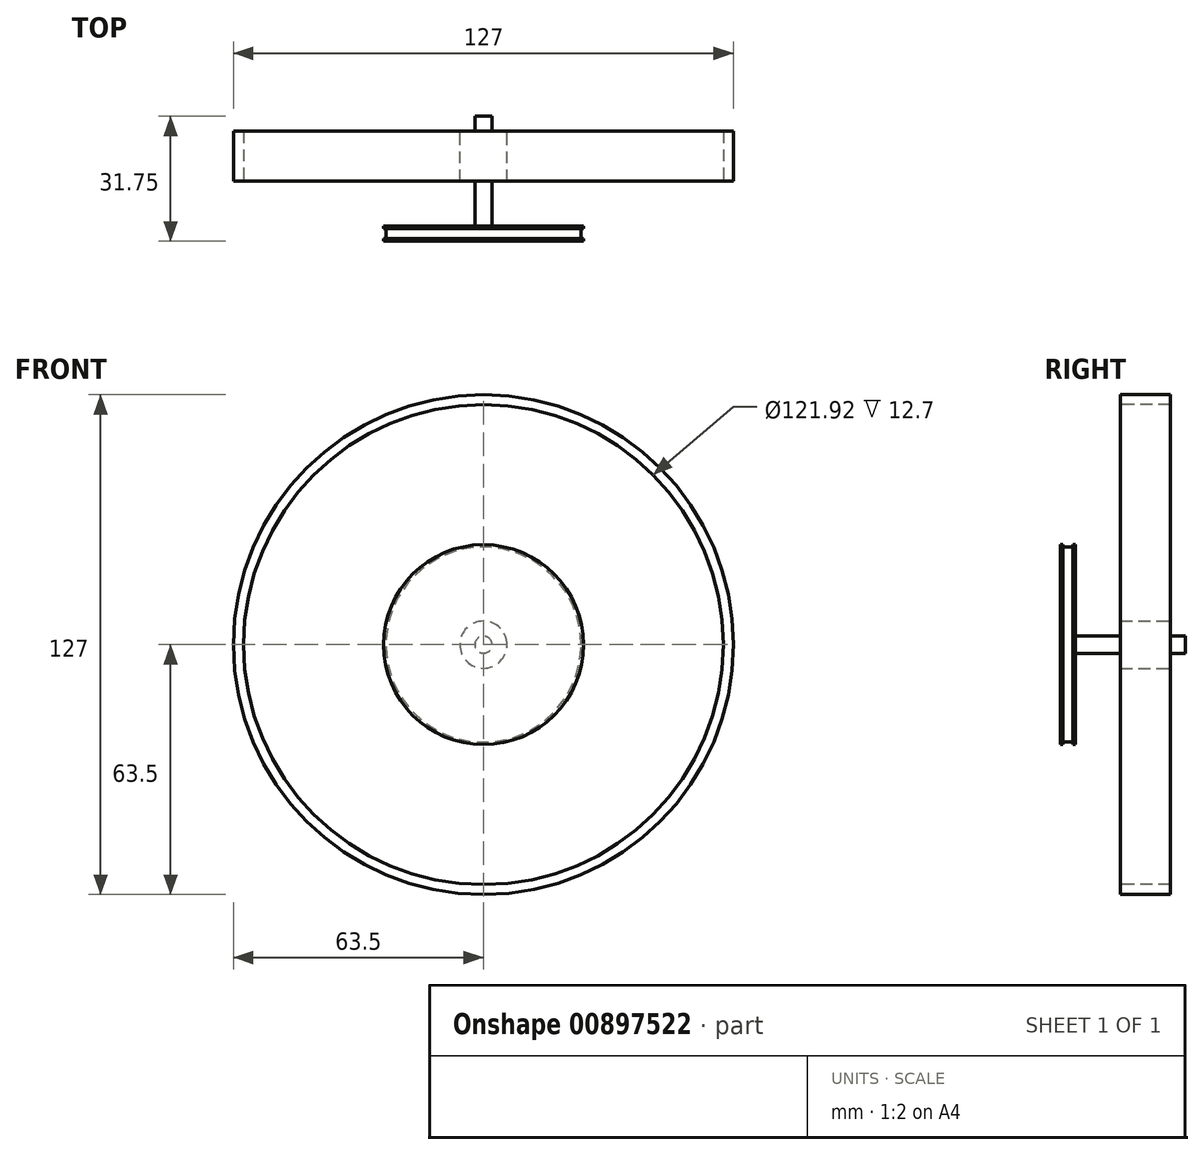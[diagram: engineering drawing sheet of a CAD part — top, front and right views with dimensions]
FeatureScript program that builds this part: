
annotation { "Feature Type Name" : "Feature", "Feature Type Description" : "" }
export const myFeature = defineFeature(function(context is Context, id is Id, definition is map)
    precondition{}
    {
        {
            var Q0;
            Q0=qCreatedBy(makeId("Front.planeOp"),FACE);
            var sketch = newSketch(context, id + "F0", { "sketchPlane" : qUnion([Q0])});
            skCircle(sketch, "E0", {"center": v(0, 0) * mm, "radius": 63.5 * mm});
            skSolve(sketch);
        }
        {
            var Q0;
            Q0 = qSketchRegion(id + "F0", true);
            extrude(context, id + "F1", {"entities" : qUnion([Q0]), "endBound" : BoundingType.SYMMETRIC, "depth" : 12.7 * mm, "offsetDistance" : 25.4 * mm});
        }
        {
            var Q0;
            Q0=makeQuery(id+"F1.opExtrude","CAP_FACE",FACE,{"disambiguationData":[OSD([sQuery(id+"F0.wireOp",EDGE,"E0")])],"isStart":false});
            var sketch = newSketch(context, id + "F2", { "sketchPlane" : qUnion([Q0])});
            skCircle(sketch, "E1.0", {"center": v(0, 0) * mm, "radius": 60.96 * mm});
            skSolve(sketch);
        }
        {
            var Q0;
            Q0 = qSketchRegion(id + "F2", true);
            extrude(context, id + "F3", {"entities" : qUnion([Q0]), "operationType" : NewBodyOperationType.REMOVE, "endBound" : BoundingType.THROUGH_ALL, "oppositeDirection" : true, "depth" : 25.4 * mm, "offsetDistance" : 25.4 * mm});
        }
        {
            var Q0;
            Q0=qCreatedBy(makeId("Front.planeOp"),FACE);
            var sketch = newSketch(context, id + "F4", { "sketchPlane" : qUnion([Q0])});
            skCircle(sketch, "E2", {"center": v(0, 0) * mm, "radius": 5.98 * mm});
            skLineSegment(sketch, "E3", {"start": v(0, 5.98) * mm, "end": v(0, 63.13) * mm});
            skLineSegment(sketch, "E4.MirrorCS", {"start": v(0, -5.98) * mm, "end": v(0, -63.13) * mm});
            skLineSegment(sketch, "E5.1.0", {"start": v(-3.64, 4.8) * mm, "end": v(-37.23, 51.04) * mm});
            skLineSegment(sketch, "E5.2.0", {"start": v(-5.88, 1.7) * mm, "end": v(-60.24, 19.37) * mm});
            skLineSegment(sketch, "E5.3.0", {"start": v(-5.88, -2.12) * mm, "end": v(-60.24, -19.78) * mm});
            skLineSegment(sketch, "E5.4.0", {"start": v(-3.64, -5.2) * mm, "end": v(-37.23, -51.45) * mm});
            skLineSegment(sketch, "E5.5.0", {"start": v(0, -6.39) * mm, "end": v(0, -63.54) * mm});
            skLineSegment(sketch, "E5.6.0", {"start": v(3.64, -5.2) * mm, "end": v(37.23, -51.45) * mm});
            skLineSegment(sketch, "E5.7.0", {"start": v(5.88, -2.12) * mm, "end": v(60.24, -19.78) * mm});
            skLineSegment(sketch, "E5.8.0", {"start": v(5.88, 1.7) * mm, "end": v(60.24, 19.37) * mm});
            skLineSegment(sketch, "E5.9.0", {"start": v(3.64, 4.8) * mm, "end": v(37.23, 51.04) * mm});
            skPoint(sketch, "E5.center", {"position": v(0, -0.2) * mm});
            skSolve(sketch);
        }
        {
            var Q0;
            Q0 = qSketchRegion(id + "F4", true);
            extrude(context, id + "F5", {"entities" : qUnion([Q0]), "endBound" : BoundingType.SYMMETRIC, "depth" : 12.7 * mm, "offsetDistance" : 25.4 * mm});
        }
        {
            var Q0;
            Q0=qCreatedBy(makeId("Front.planeOp"),FACE);
            var sketch = newSketch(context, id + "F6", { "sketchPlane" : qUnion([Q0])});
            skCircle(sketch, "E6.0", {"center": v(0, 0) * mm, "radius": 2.17 * mm});
            skSolve(sketch);
        }
        {
            var Q0;
            Q0 = qSketchRegion(id + "F6", true);
            extrude(context, id + "F7", {"entities" : qUnion([Q0]), "operationType" : NewBodyOperationType.ADD, "depth" : 17.78 * mm, "offsetDistance" : 25.4 * mm, "hasSecondDirection" : true, "secondDirectionOppositeDirection" : true, "secondDirectionDepth" : 10.16 * mm});
        }
        {
            var Q0;
            Q0=makeQuery(id+"F7.opExtrude","CAP_FACE",FACE,{"disambiguationData":[OSD([sQuery(id+"F6.wireOp",EDGE,"E6.0")])],"isStart":false});
            var sketch = newSketch(context, id + "F8", { "sketchPlane" : qUnion([Q0])});
            skCircle(sketch, "E7", {"center": v(0, 0) * mm, "radius": 25.4 * mm});
            skSolve(sketch);
        }
        {
            var Q0;
            Q0 = qSketchRegion(id + "F8", true);
            extrude(context, id + "F9", {"entities" : qUnion([Q0]), "operationType" : NewBodyOperationType.ADD, "depth" : 0.64 * mm, "offsetDistance" : 25.4 * mm});
        }
        {
            var Q0;
            Q0=makeQuery(id+"F9.opExtrude","CAP_FACE",FACE,{"disambiguationData":[OSD([sQuery(id+"F8.wireOp",EDGE,"E7")])],"isStart":false});
            var sketch = newSketch(context, id + "F10", { "sketchPlane" : qUnion([Q0])});
            skCircle(sketch, "E8", {"center": v(0, 0) * mm, "radius": 24.76 * mm});
            skSolve(sketch);
        }
        {
            var Q0;
            Q0 = qSketchRegion(id + "F10", true);
            extrude(context, id + "F11", {"entities" : qUnion([Q0]), "operationType" : NewBodyOperationType.ADD, "depth" : 2.54 * mm, "offsetDistance" : 25.4 * mm});
        }
        {
            var Q0;
            Q0=sQuery(id+"F4.wireOp",EDGE,"E5.9.0");
            var Q1;
            Q1=sQuery(id+"F4.wireOp",EDGE,"E5.8.0");
            var Q2;
            Q2=sQuery(id+"F4.wireOp",EDGE,"E5.7.0");
            var Q3;
            Q3=sQuery(id+"F4.wireOp",EDGE,"E5.6.0");
            var Q4;
            Q4=sQuery(id+"F4.wireOp",EDGE,"E5.5.0");
            var Q5;
            Q5=sQuery(id+"F4.wireOp",EDGE,"E5.4.0");
            var Q6;
            Q6=sQuery(id+"F4.wireOp",EDGE,"E5.3.0");
            var Q7;
            Q7=sQuery(id+"F4.wireOp",EDGE,"E5.2.0");
            var Q8;
            Q8=sQuery(id+"F4.wireOp",EDGE,"E5.1.0");
            var Q9;
            Q9=sQuery(id+"F4.wireOp",EDGE,"E3");
            extrude(context, id + "F12", {"bodyType" : ToolBodyType.SURFACE, "surfaceEntities" : qUnion([Q0, Q1, Q2, Q3, Q4, Q5, Q6, Q7, Q8, Q9]), "endBound" : BoundingType.SYMMETRIC, "depth" : 0.25 * mm, "offsetDistance" : 25.4 * mm});
        }
        {
            var Q0;
            Q0=makeQuery(id+"F11.opExtrude","CAP_FACE",FACE,{"disambiguationData":[OSD([sQuery(id+"F10.wireOp",EDGE,"E8")])],"isStart":false});
            var sketch = newSketch(context, id + "F13", { "sketchPlane" : qUnion([Q0])});
            skCircle(sketch, "E9", {"center": v(0, 0) * mm, "radius": 25.4 * mm});
            skSolve(sketch);
        }
        {
            var Q0;
            Q0 = qSketchRegion(id + "F13", true);
            extrude(context, id + "F14", {"entities" : qUnion([Q0]), "operationType" : NewBodyOperationType.ADD, "depth" : 0.64 * mm, "offsetDistance" : 25.4 * mm});
        }
    });
